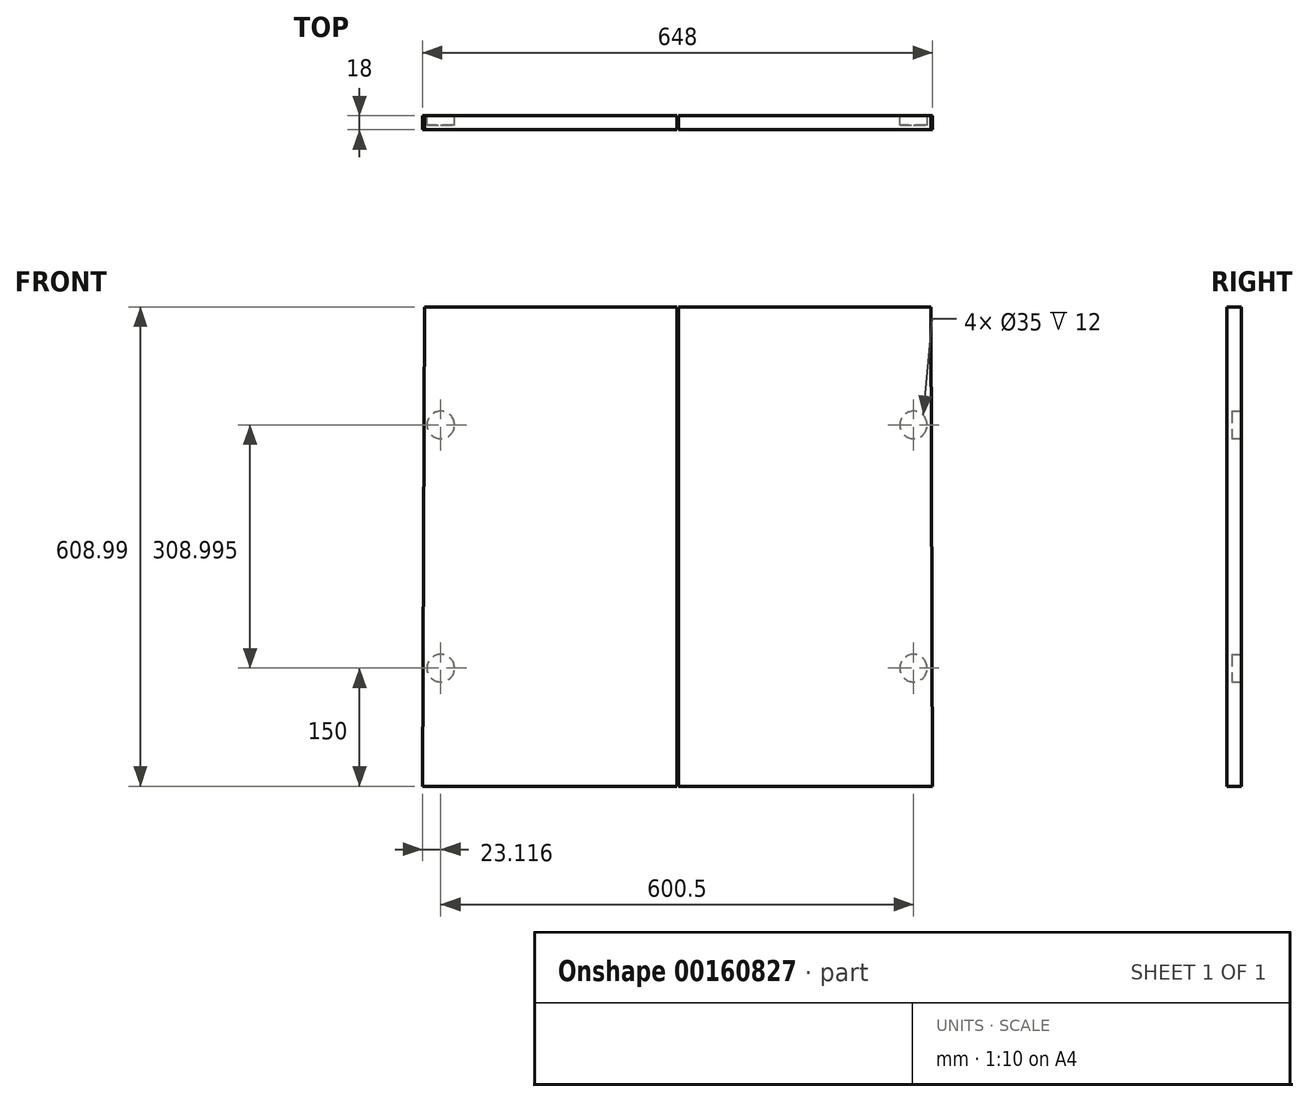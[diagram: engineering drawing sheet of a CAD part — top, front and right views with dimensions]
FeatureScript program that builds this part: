
annotation { "Feature Type Name" : "Feature", "Feature Type Description" : "" }
export const myFeature = defineFeature(function(context is Context, id is Id, definition is map)
    precondition{}
    {
        {
            var Q0;
            Q0=qCreatedBy(makeId("Front.planeOp"),FACE);
            var sketch = newSketch(context, id + "F0", { "sketchPlane" : qUnion([Q0])});
            skLineSegment(sketch, "E0", {"start": v(0, 0) * mm, "end": v(0, 730.12) * mm, "construction": true});
            skLineSegment(sketch, "E1", {"start": v(1, 609) * mm, "end": v(1, 0) * mm});
            skLineSegment(sketch, "E2", {"start": v(1, 0) * mm, "end": v(324, 0) * mm});
            skLineSegment(sketch, "E3", {"start": v(324, 0) * mm, "end": v(321.5, 609) * mm});
            skLineSegment(sketch, "E4", {"start": v(321.5, 609) * mm, "end": v(1, 609) * mm});
            skLineSegment(sketch, "E5", {"start": v(-1, 0) * mm, "end": v(-324, 0) * mm});
            skLineSegment(sketch, "E6", {"start": v(-324, 0) * mm, "end": v(-321.5, 609) * mm});
            skLineSegment(sketch, "E7", {"start": v(-321.5, 609) * mm, "end": v(-1, 609) * mm});
            skLineSegment(sketch, "E8", {"start": v(-1, 609) * mm, "end": v(-1, 0) * mm});
            skSolve(sketch);
        }
        {
            var Q0;
            Q0 = qSketchRegion(id + "F0", true);
            extrude(context, id + "F1", {"entities" : qUnion([Q0]), "depth" : 18 * mm});
        }
        {
            var Q0;
            Q0=makeQuery(id+"F1.opExtrude","CAP_FACE",FACE,{"disambiguationData":[OSD([sQuery(id+"F0.wireOp",EDGE,"E1"),sQuery(id+"F0.wireOp",EDGE,"E2"),sQuery(id+"F0.wireOp",EDGE,"E3"),sQuery(id+"F0.wireOp",EDGE,"E4")])],"isStart":true});
            var sketch = newSketch(context, id + "F2", { "sketchPlane" : qUnion([Q0])});
            skCircle(sketch, "E9", {"center": v(-299.62, 459) * mm, "radius": 17.5 * mm});
            skCircle(sketch, "E10", {"center": v(-299.62, 150) * mm, "radius": 17.5 * mm});
            skCircle(sketch, "E11", {"center": v(300.88, 459) * mm, "radius": 17.5 * mm});
            skCircle(sketch, "E12", {"center": v(300.88, 150) * mm, "radius": 17.5 * mm});
            skSolve(sketch);
        }
        {
            var Q0;
            Q0 = qSketchRegion(id + "F2", true);
            extrude(context, id + "F3", {"entities" : qUnion([Q0]), "operationType" : NewBodyOperationType.REMOVE, "oppositeDirection" : true, "depth" : 12 * mm});
        }
    });
